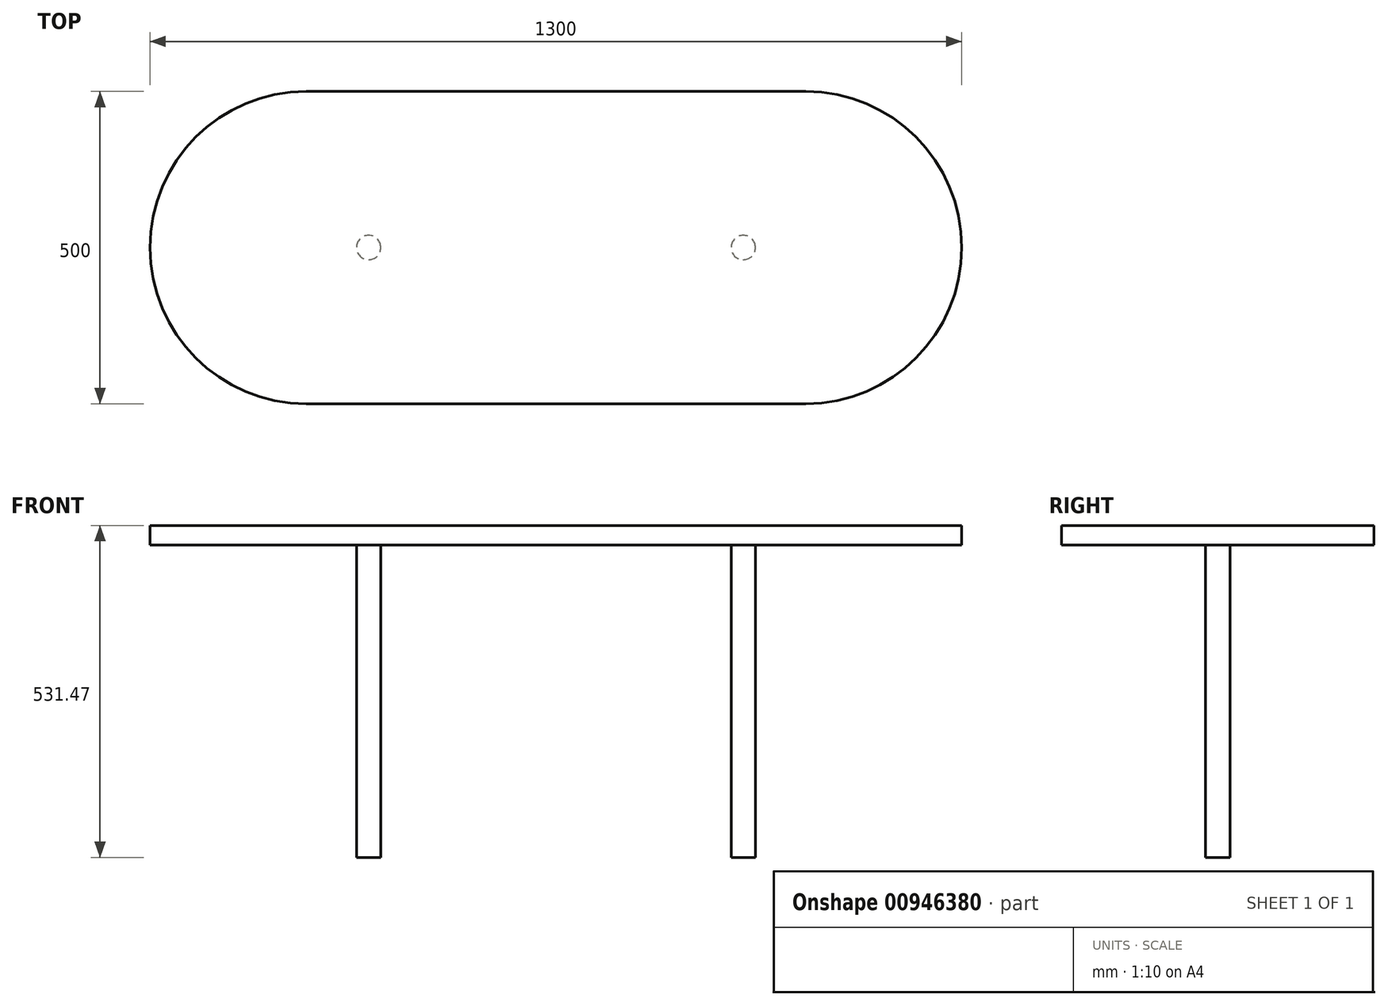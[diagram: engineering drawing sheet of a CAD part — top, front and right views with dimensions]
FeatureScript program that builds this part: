
annotation { "Feature Type Name" : "Feature", "Feature Type Description" : "" }
export const myFeature = defineFeature(function(context is Context, id is Id, definition is map)
    precondition{}
    {
        {
            var Q0;
            Q0=qCreatedBy(makeId("Top.planeOp"),FACE);
            var sketch = newSketch(context, id + "F0", { "sketchPlane" : qUnion([Q0])});
            skLineSegment(sketch, "E0.bottom", {"start": v(-300, 250) * mm, "end": v(300, 250) * mm});
            skLineSegment(sketch, "E0.top", {"start": v(-300, -250) * mm, "end": v(300, -250) * mm});
            skLineSegment(sketch, "E0.left", {"start": v(-300, 250) * mm, "end": v(-300, -250) * mm});
            skLineSegment(sketch, "E0.right", {"start": v(300, 250) * mm, "end": v(300, -250) * mm});
            skPoint(sketch, "E0.middle", {"position": v(0, 0) * mm});
            skPoint(sketch, "E1.center.orphan", {"position": v(300, 0) * mm});
            skPoint(sketch, "E2.center.orphan", {"position": v(-300, 0) * mm});
            skLineSegment(sketch, "E3", {"start": v(300, 250) * mm, "end": v(400, 250) * mm});
            skLineSegment(sketch, "E4", {"start": v(300, -250) * mm, "end": v(400, -250) * mm});
            skLineSegment(sketch, "E5", {"start": v(-300, -250) * mm, "end": v(-400, -250) * mm});
            skLineSegment(sketch, "E6", {"start": v(-300, 250) * mm, "end": v(-400, 250) * mm});
            skArc(sketch, "E7", {"start": v(400, 250) * mm, "mid": v(650, 0) * mm, "end": v(400, -250) * mm});
            skArc(sketch, "E8", {"start": v(-400, 250) * mm, "mid": v(-650, 0) * mm, "end": v(-400, -250) * mm});
            skSolve(sketch);
        }
        {
            var Q0;
            Q0=makeQuery(id+"F0.imprint","IMPRINT",FACE,{"disambiguationData":[TD([[makeQuery(id+"F0.imprint","IMPRINT",EDGE,{"derivedFrom":sQuery(id+"F0.wireOp",EDGE,"E0.left")}),-1.0]])]});
            var Q1;
            Q1=makeQuery(id+"F0.imprint","IMPRINT",FACE,{"disambiguationData":[TD([[makeQuery(id+"F0.imprint","IMPRINT",EDGE,{"derivedFrom":sQuery(id+"F0.wireOp",EDGE,"E0.bottom")}),-1.0]])]});
            var Q2;
            Q2=makeQuery(id+"F0.imprint","IMPRINT",FACE,{"disambiguationData":[TD([[makeQuery(id+"F0.imprint","IMPRINT",EDGE,{"derivedFrom":sQuery(id+"F0.wireOp",EDGE,"E0.right")}),1.0]])]});
            extrude(context, id + "F1", {"entities" : qUnion([Q0, Q1, Q2]), "depth" : 31.47 * mm, "offsetDistance" : 25 * mm});
        }
        {
            var Q0;
            Q0=qCreatedBy(makeId("Top.planeOp"),FACE);
            var sketch = newSketch(context, id + "F2", { "sketchPlane" : qUnion([Q0])});
            skLineSegment(sketch, "E9.0", {"start": v(300, 250) * mm, "end": v(300, -250) * mm});
            skLineSegment(sketch, "E10.0", {"start": v(-300, 250) * mm, "end": v(-300, -250) * mm});
            skCircle(sketch, "E11", {"center": v(-300, 0) * mm, "radius": 19.5 * mm});
            skCircle(sketch, "E12", {"center": v(300, 0) * mm, "radius": 19.5 * mm});
            skSolve(sketch);
        }
        {
            var Q0;
            {var subQ0=sQuery(id+"F2.wireOp",EDGE,"E11");var subQ1=sQuery(id+"F2.wireOp",EDGE,"E10.0");var subQ2=makeQuery(id+"F2.imprint","INTERSECT",VERTEX,{"disambiguationData":[OD(0.0)],"derivedFrom":[subQ1,subQ0]});Q0=makeQuery(id+"F2.imprint","IMPRINT",FACE,{"disambiguationData":[TD([[makeQuery(id+"F2.imprint","IMPRINT",EDGE,{"disambiguationData":[TD([[subQ2,1.0]])],"derivedFrom":subQ1}),1.0]])]});}
            var Q1;
            {var subQ0=sQuery(id+"F2.wireOp",EDGE,"E11");var subQ1=sQuery(id+"F2.wireOp",EDGE,"E10.0");var subQ2=makeQuery(id+"F2.imprint","INTERSECT",VERTEX,{"disambiguationData":[OD(0.0)],"derivedFrom":[subQ1,subQ0]});Q1=makeQuery(id+"F2.imprint","IMPRINT",FACE,{"disambiguationData":[TD([[makeQuery(id+"F2.imprint","IMPRINT",EDGE,{"disambiguationData":[TD([[subQ2,1.0]])],"derivedFrom":subQ1}),-1.0]])]});}
            var Q2;
            {var subQ0=sQuery(id+"F2.wireOp",EDGE,"E12");var subQ1=sQuery(id+"F2.wireOp",EDGE,"E9.0");var subQ2=makeQuery(id+"F2.imprint","INTERSECT",VERTEX,{"disambiguationData":[OD(0.0)],"derivedFrom":[subQ1,subQ0]});Q2=makeQuery(id+"F2.imprint","IMPRINT",FACE,{"disambiguationData":[TD([[makeQuery(id+"F2.imprint","IMPRINT",EDGE,{"disambiguationData":[TD([[subQ2,1.0]])],"derivedFrom":subQ1}),1.0]])]});}
            var Q3;
            {var subQ0=sQuery(id+"F2.wireOp",EDGE,"E12");var subQ1=sQuery(id+"F2.wireOp",EDGE,"E9.0");var subQ2=makeQuery(id+"F2.imprint","INTERSECT",VERTEX,{"disambiguationData":[OD(0.0)],"derivedFrom":[subQ1,subQ0]});Q3=makeQuery(id+"F2.imprint","IMPRINT",FACE,{"disambiguationData":[TD([[makeQuery(id+"F2.imprint","IMPRINT",EDGE,{"disambiguationData":[TD([[subQ2,1.0]])],"derivedFrom":subQ1}),-1.0]])]});}
            extrude(context, id + "F3", {"entities" : qUnion([Q0, Q1, Q2, Q3]), "operationType" : NewBodyOperationType.ADD, "oppositeDirection" : true, "depth" : 500 * mm, "offsetDistance" : 25 * mm});
        }
    });
